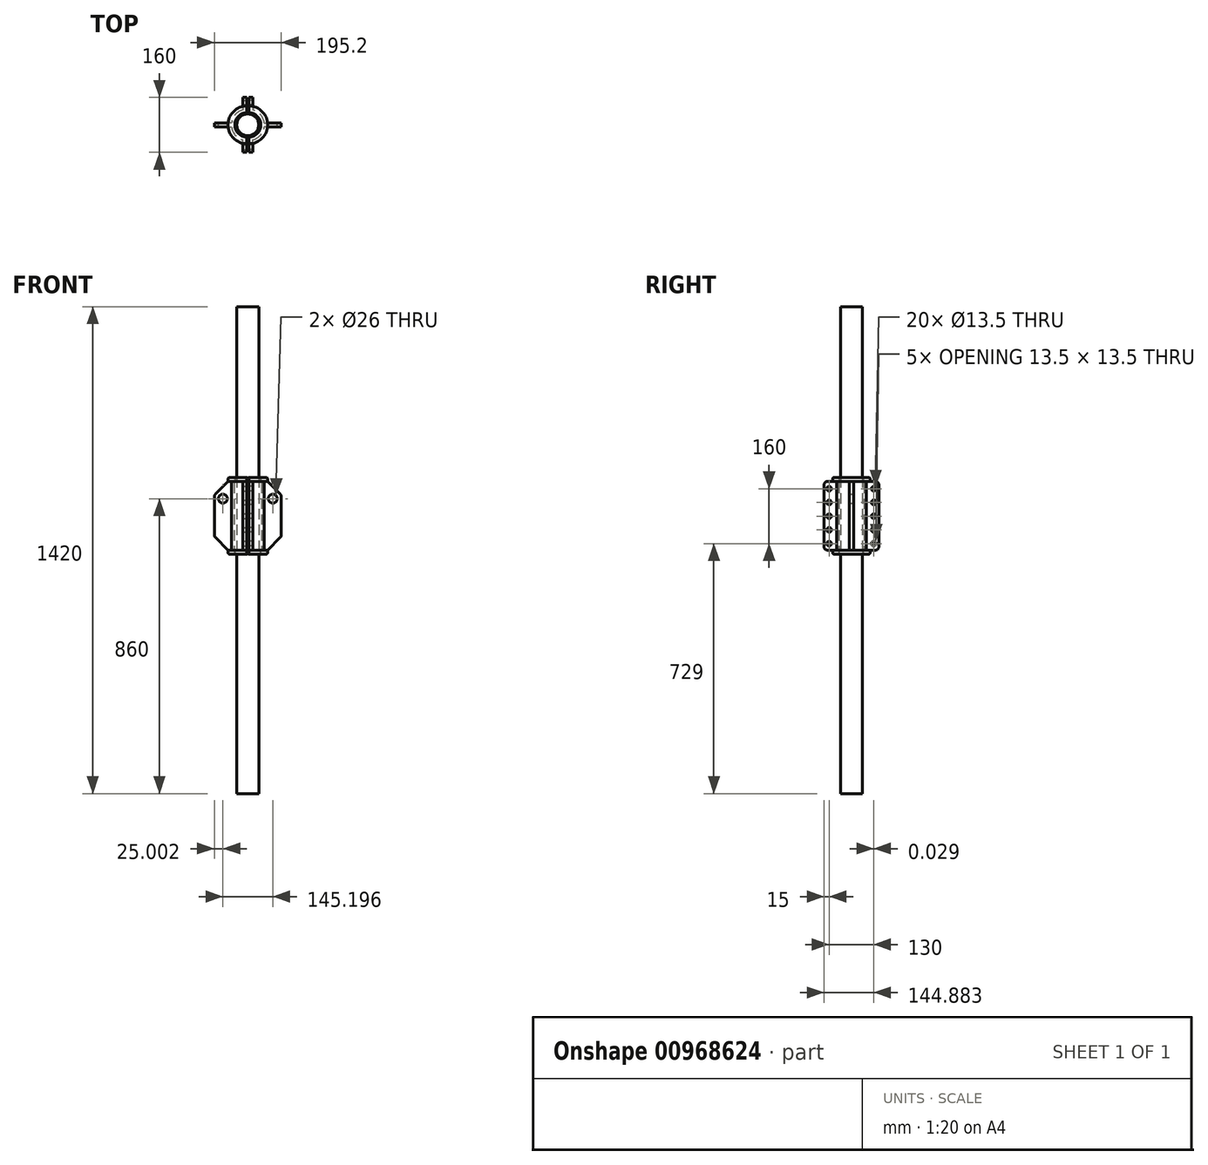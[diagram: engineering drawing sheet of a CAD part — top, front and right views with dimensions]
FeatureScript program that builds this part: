
annotation { "Feature Type Name" : "Feature", "Feature Type Description" : "" }
export const myFeature = defineFeature(function(context is Context, id is Id, definition is map)
    precondition{}
    {
        {
            var Q0;
            Q0=qCreatedBy(makeId("Top.planeOp"),FACE);
            var sketch = newSketch(context, id + "F0", { "sketchPlane" : qUnion([Q0])});
            skArc(sketch, "E0", {"start": v(0, -37) * mm, "mid": v(37, 0) * mm, "end": v(0, 37) * mm});
            skArc(sketch, "E1", {"start": v(0, -45) * mm, "mid": v(45, 0) * mm, "end": v(0, 45) * mm});
            skLineSegment(sketch, "E2", {"start": v(0, 45) * mm, "end": v(0, 37) * mm});
            skLineSegment(sketch, "E3", {"start": v(0, -37) * mm, "end": v(0, -45) * mm});
            skLineSegment(sketch, "E4", {"start": v(0, 45) * mm, "end": v(0, 80) * mm});
            skLineSegment(sketch, "E5", {"start": v(0, 80) * mm, "end": v(12, 80) * mm});
            skLineSegment(sketch, "E6", {"start": v(12, 80) * mm, "end": v(12, 43.37) * mm});
            skLineSegment(sketch, "E7", {"start": v(0, -45) * mm, "end": v(0, -80) * mm});
            skLineSegment(sketch, "E8", {"start": v(0, -80) * mm, "end": v(12, -80) * mm});
            skLineSegment(sketch, "E9", {"start": v(12, -80) * mm, "end": v(12, -43.37) * mm});
            skLineSegment(sketch, "E10", {"start": v(44.6, 6) * mm, "end": v(94.6, 6) * mm});
            skLineSegment(sketch, "E11", {"start": v(94.6, 6) * mm, "end": v(94.6, -6) * mm});
            skLineSegment(sketch, "E12", {"start": v(94.6, -6) * mm, "end": v(44.6, -6) * mm});
            skSolve(sketch);
        }
        {
            var Q0;
            Q0=makeQuery(id+"F0.imprint","IMPRINT",FACE,{"disambiguationData":[TD([[makeQuery(id+"F0.imprint","IMPRINT",EDGE,{"derivedFrom":sQuery(id+"F0.wireOp",EDGE,"E0")}),-1.0]])]});
            var Q1;
            {var subQ0=sQuery(id+"F0.wireOp",EDGE,"E4");Q1=makeQuery(id+"F0.imprint","IMPRINT",FACE,{"disambiguationData":[TD([[makeQuery(id+"F0.imprint","IMPRINT",EDGE,{"derivedFrom":subQ0}),-1.0]])]});}
            var Q2;
            {var subQ0=sQuery(id+"F0.wireOp",EDGE,"E10");Q2=makeQuery(id+"F0.imprint","IMPRINT",FACE,{"disambiguationData":[TD([[makeQuery(id+"F0.imprint","IMPRINT",EDGE,{"derivedFrom":subQ0}),-1.0]])]});}
            var Q3;
            {var subQ0=sQuery(id+"F0.wireOp",EDGE,"E7");Q3=makeQuery(id+"F0.imprint","IMPRINT",FACE,{"disambiguationData":[TD([[makeQuery(id+"F0.imprint","IMPRINT",EDGE,{"derivedFrom":subQ0}),1.0]])]});}
            extrude(context, id + "F1", {"entities" : qUnion([Q0, Q1, Q2, Q3]), "depth" : 200 * mm, "offsetDistance" : 25 * mm});
        }
        {
            var Q0;
            Q0=qCreatedBy(makeId("Right.planeOp"),FACE);
            var sketch = newSketch(context, id + "F2", { "sketchPlane" : qUnion([Q0])});
            skLineSegment(sketch, "E13", {"start": v(-65, 179) * mm, "end": v(-65, -10.82) * mm});
            skCircle(sketch, "E14", {"center": v(-65, 179) * mm, "radius": 7 * mm});
            skCircle(sketch, "E15.1.0.0", {"center": v(-64.97, 139) * mm, "radius": 7 * mm});
            skCircle(sketch, "E15.2.0.0", {"center": v(-64.94, 99) * mm, "radius": 7 * mm});
            skCircle(sketch, "E15.3.0.0", {"center": v(-64.91, 59) * mm, "radius": 7 * mm});
            skCircle(sketch, "E15.4.0.0", {"center": v(-64.88, 19) * mm, "radius": 7 * mm});
            skLineSegment(sketch, "E15.direction1", {"start": v(-65, 179) * mm, "end": v(-64.97, 139) * mm, "construction": true});
            skCircle(sketch, "E16.MirrorC", {"center": v(64.88, 19) * mm, "radius": 7 * mm});
            skCircle(sketch, "E17.MirrorC", {"center": v(64.91, 59) * mm, "radius": 7 * mm});
            skCircle(sketch, "E18.MirrorC", {"center": v(64.94, 99) * mm, "radius": 7 * mm});
            skCircle(sketch, "E19.MirrorC", {"center": v(64.97, 139) * mm, "radius": 7 * mm});
            skCircle(sketch, "E20.MirrorC", {"center": v(65, 179) * mm, "radius": 7 * mm});
            skSolve(sketch);
        }
        {
            var Q0;
            Q0=sQuery(id+"F2.wireOp",VERTEX,"E13.start");
            var Q1;
            Q1=sQuery(id+"F2.wireOp",VERTEX,"E15.direction1.end");
            var Q2;
            Q2=sQuery(id+"F2.wireOp",VERTEX,"E15.2.0.0.center");
            var Q3;
            Q3=sQuery(id+"F2.wireOp",VERTEX,"E15.3.0.0.center");
            var Q4;
            Q4=sQuery(id+"F2.wireOp",VERTEX,"E15.4.0.0.center");
            var Q5;
            Q5=sQuery(id+"F2.wireOp",VERTEX,"E20.MirrorC.center");
            var Q6;
            Q6=sQuery(id+"F2.wireOp",VERTEX,"E19.MirrorC.center");
            var Q7;
            Q7=sQuery(id+"F2.wireOp",VERTEX,"E18.MirrorC.center");
            var Q8;
            Q8=sQuery(id+"F2.wireOp",VERTEX,"E17.MirrorC.center");
            var Q9;
            Q9=sQuery(id+"F2.wireOp",VERTEX,"E16.MirrorC.center");
            var Q10;
            Q10=makeQuery(id+"F1.opExtrude","SWEPT_BODY",BODY,{"disambiguationData":[OSD([sQuery(id+"F0.wireOp",EDGE,"E0"),sQuery(id+"F0.wireOp",EDGE,"E1"),sQuery(id+"F0.wireOp",EDGE,"E2"),sQuery(id+"F0.wireOp",EDGE,"E3"),sQuery(id+"F0.wireOp",EDGE,"E4"),sQuery(id+"F0.wireOp",EDGE,"E5"),sQuery(id+"F0.wireOp",EDGE,"E6"),sQuery(id+"F0.wireOp",EDGE,"E7"),sQuery(id+"F0.wireOp",EDGE,"E8"),sQuery(id+"F0.wireOp",EDGE,"E9"),sQuery(id+"F0.wireOp",EDGE,"E10"),sQuery(id+"F0.wireOp",EDGE,"E11"),sQuery(id+"F0.wireOp",EDGE,"E12")])]});
            hole(context, id + "F3", {"style" : HoleStyle.SIMPLE, "endStyle" : HoleEndStyle.THROUGH, "oppositeDirection" : true, "standardTappedOrClearance" : lookupTablePath({ "fit" : "Normal", "standard" : "ISO", "size" : "M12", "type" : "Clearance" }), "standardBlindInLast" : lookupTablePath({ "fit" : "Normal", "standard" : "ISO", "engagement" : "75%", "pitch" : "1.75 mm", "size" : "M12", "type" : "Clearance & tapped" }), "holeDiameter" : 13.5 * mm, "majorDiameter" : 5 * mm, "isTappedThrough" : true, "tappedDepth" : 14.75 * mm, "tapClearance" : 3, "locations" : qUnion([Q0, Q1, Q2, Q3, Q4, Q5, Q6, Q7, Q8, Q9]), "scope" : qUnion([Q10])});
        }
        {
            var Q0;
            Q0=makeQuery(id+"F1.opExtrude","CAP_EDGE",EDGE,{"disambiguationData":[OSD([sQuery(id+"F0.wireOp",EDGE,"E11")])],"isStart":false});
            var Q1;
            Q1=makeQuery(id+"F1.opExtrude","CAP_EDGE",EDGE,{"disambiguationData":[OSD([sQuery(id+"F0.wireOp",EDGE,"E11")])],"isStart":true});
            chamfer(context, id + "F4", {"entities" : qUnion([Q0, Q1]), "width" : 40 * mm, "tangentPropagation" : true});
        }
        {
            var Q0;
            Q0=makeQuery(id+"F1.opExtrude","SWEPT_FACE",FACE,{"disambiguationData":[OSD([sQuery(id+"F0.wireOp",EDGE,"E10")])]});
            var sketch = newSketch(context, id + "F5", { "sketchPlane" : qUnion([Q0])});
            skCircle(sketch, "E21", {"center": v(-69.6, 150) * mm, "radius": 13 * mm});
            skSolve(sketch);
        }
        {
            var Q0;
            {var subQ0=sQuery(id+"F0.wireOp",EDGE,"E11");Q0=makeQuery(id+"F4.opChamfer","BLEND_EDGE",EDGE,{"blendedFrom":[makeQuery(id+"F1.opExtrude","CAP_EDGE",EDGE,{"disambiguationData":[OSD([subQ0])],"isStart":false}),makeQuery(id+"F1.opExtrude","SWEPT_FACE",FACE,{"disambiguationData":[OSD([subQ0])]})],"blendedInto":[makeQuery(id+"F1.opExtrude","SWEPT_FACE",FACE,{"disambiguationData":[OSD([subQ0])]})]});}
            var Q1;
            {var subQ0=sQuery(id+"F0.wireOp",EDGE,"E11");Q1=makeQuery(id+"F4.opChamfer","BLEND_EDGE",EDGE,{"blendedFrom":[makeQuery(id+"F1.opExtrude","CAP_EDGE",EDGE,{"disambiguationData":[OSD([subQ0])],"isStart":true}),makeQuery(id+"F1.opExtrude","SWEPT_FACE",FACE,{"disambiguationData":[OSD([subQ0])]})],"blendedInto":[makeQuery(id+"F1.opExtrude","SWEPT_FACE",FACE,{"disambiguationData":[OSD([subQ0])]})]});}
            fillet(context, id + "F6", {"entities" : qUnion([Q0, Q1]), "radius" : 10 * mm, "tangentPropagation" : true, "allowEdgeOverflow" : false});
        }
        {
            var Q0;
            Q0=qCreatedBy(makeId("Top.planeOp"),FACE);
            var sketch = newSketch(context, id + "F7", { "sketchPlane" : qUnion([Q0])});
            skArc(sketch, "E22", {"start": v(0, -55) * mm, "mid": v(55, 0) * mm, "end": v(0, 55) * mm});
            skArc(sketch, "E23", {"start": v(0, -35) * mm, "mid": v(35, 0) * mm, "end": v(0, 35) * mm});
            skLineSegment(sketch, "E24", {"start": v(0, -35) * mm, "end": v(0, -55) * mm});
            skLineSegment(sketch, "E25", {"start": v(0, 55) * mm, "end": v(0, 35) * mm});
            skSolve(sketch);
        }
        {
            var Q0;
            Q0=makeQuery(id+"F7.imprint","IMPRINT",FACE,{"disambiguationData":[TD([[makeQuery(id+"F7.imprint","IMPRINT",EDGE,{"derivedFrom":sQuery(id+"F7.wireOp",EDGE,"E22")}),1.0]])]});
            extrude(context, id + "F8", {"entities" : qUnion([Q0]), "operationType" : NewBodyOperationType.ADD, "oppositeDirection" : true, "depth" : 12 * mm, "offsetDistance" : 25 * mm});
        }
        {
            var Q0;
            Q0=makeQuery(id+"F1.opExtrude","CAP_FACE",FACE,{"disambiguationData":[OSD([sQuery(id+"F0.wireOp",EDGE,"E0"),sQuery(id+"F0.wireOp",EDGE,"E1"),sQuery(id+"F0.wireOp",EDGE,"E2"),sQuery(id+"F0.wireOp",EDGE,"E3"),sQuery(id+"F0.wireOp",EDGE,"E4"),sQuery(id+"F0.wireOp",EDGE,"E5"),sQuery(id+"F0.wireOp",EDGE,"E6"),sQuery(id+"F0.wireOp",EDGE,"E7"),sQuery(id+"F0.wireOp",EDGE,"E8"),sQuery(id+"F0.wireOp",EDGE,"E9"),sQuery(id+"F0.wireOp",EDGE,"E10"),sQuery(id+"F0.wireOp",EDGE,"E11"),sQuery(id+"F0.wireOp",EDGE,"E12")])],"isStart":false});
            cPlane(context, id + "F9", {"entities" : qUnion([Q0]), "cplaneType" : CPlaneType.OFFSET, "offset" : 0 * mm, "width" : 150 * mm, "height" : 150 * mm});
        }
        {
            var Q0;
            Q0=qCreatedBy(id+"F9.planeOp",FACE);
            var sketch = newSketch(context, id + "F10", { "sketchPlane" : qUnion([Q0])});
            skArc(sketch, "E26", {"start": v(0, -55) * mm, "mid": v(55, 0) * mm, "end": v(0, 55) * mm});
            skArc(sketch, "E27", {"start": v(0, -35) * mm, "mid": v(35, 0) * mm, "end": v(0, 35) * mm});
            skLineSegment(sketch, "E28", {"start": v(0, -35) * mm, "end": v(0, -55) * mm});
            skLineSegment(sketch, "E29", {"start": v(0, 55) * mm, "end": v(0, 35) * mm});
            skSolve(sketch);
        }
        {
            var Q0;
            Q0=makeQuery(id+"F10.imprint","IMPRINT",FACE,{"disambiguationData":[TD([[makeQuery(id+"F10.imprint","IMPRINT",EDGE,{"derivedFrom":sQuery(id+"F10.wireOp",EDGE,"E26")}),1.0]])]});
            extrude(context, id + "F11", {"entities" : qUnion([Q0]), "operationType" : NewBodyOperationType.ADD, "depth" : 12 * mm, "offsetDistance" : 25 * mm});
        }
        {
            var Q0;
            Q0=sQuery(id+"F5.wireOp",VERTEX,"E21.center");
            var Q1;
            Q1=makeQuery(id+"F1.opExtrude","SWEPT_BODY",BODY,{"disambiguationData":[OSD([sQuery(id+"F0.wireOp",EDGE,"E0"),sQuery(id+"F0.wireOp",EDGE,"E1"),sQuery(id+"F0.wireOp",EDGE,"E2"),sQuery(id+"F0.wireOp",EDGE,"E3"),sQuery(id+"F0.wireOp",EDGE,"E4"),sQuery(id+"F0.wireOp",EDGE,"E5"),sQuery(id+"F0.wireOp",EDGE,"E6"),sQuery(id+"F0.wireOp",EDGE,"E7"),sQuery(id+"F0.wireOp",EDGE,"E8"),sQuery(id+"F0.wireOp",EDGE,"E9"),sQuery(id+"F0.wireOp",EDGE,"E10"),sQuery(id+"F0.wireOp",EDGE,"E11"),sQuery(id+"F0.wireOp",EDGE,"E12")])]});
            hole(context, id + "F12", {"style" : HoleStyle.SIMPLE, "endStyle" : HoleEndStyle.THROUGH, "standardTappedOrClearance" : lookupTablePath({ "fit" : "Normal", "standard" : "ISO", "size" : "M24", "type" : "Clearance" }), "standardBlindInLast" : lookupTablePath({ "fit" : "Normal", "standard" : "ISO", "engagement" : "75%", "pitch" : "2 mm", "size" : "M24", "type" : "Clearance & tapped" }), "holeDiameter" : 26 * mm, "majorDiameter" : 5 * mm, "isTappedThrough" : true, "tappedDepth" : 14.75 * mm, "tapClearance" : 3, "locations" : qUnion([Q0]), "scope" : qUnion([Q1])});
        }
        {
            var Q0;
            Q0=makeQuery(id+"F1.opExtrude","CAP_EDGE",EDGE,{"disambiguationData":[OSD([sQuery(id+"F0.wireOp",EDGE,"E8")])],"isStart":false});
            var Q1;
            Q1=makeQuery(id+"F1.opExtrude","CAP_EDGE",EDGE,{"disambiguationData":[OSD([sQuery(id+"F0.wireOp",EDGE,"E5")])],"isStart":false});
            var Q2;
            Q2=makeQuery(id+"F1.opExtrude","CAP_EDGE",EDGE,{"disambiguationData":[OSD([sQuery(id+"F0.wireOp",EDGE,"E5")])],"isStart":true});
            var Q3;
            Q3=makeQuery(id+"F1.opExtrude","CAP_EDGE",EDGE,{"disambiguationData":[OSD([sQuery(id+"F0.wireOp",EDGE,"E8")])],"isStart":true});
            fillet(context, id + "F13", {"entities" : qUnion([Q0, Q1, Q2, Q3]), "radius" : 10 * mm, "tangentPropagation" : true, "allowEdgeOverflow" : false});
        }
        {
            var Q0;
            {var subQ0=makeQuery(id+"F1.opExtrude","CAP_EDGE",EDGE,{"disambiguationData":[OSD([sQuery(id+"F0.wireOp",EDGE,"E0")])],"isStart":false});Q0=makeQuery(id+"FrsH2Kbrjr3JI1j_1.boolean.opBoolean","MERGE",EDGE,{"derivedFrom":[subQ0,makeQuery(id+"FrsH2Kbrjr3JI1j_1.opPattern","COPY",EDGE,{"derivedFrom":subQ0,"instanceName":"1"})]});}
            var Q1;
            {var subQ0=makeQuery(id+"F11.opExtrude","CAP_EDGE",EDGE,{"disambiguationData":[OSD([sQuery(id+"F10.wireOp",EDGE,"E27")])],"isStart":false});Q1=makeQuery(id+"FrsH2Kbrjr3JI1j_1.boolean.opBoolean","MERGE",EDGE,{"derivedFrom":[subQ0,makeQuery(id+"FrsH2Kbrjr3JI1j_1.opPattern","COPY",EDGE,{"derivedFrom":subQ0,"instanceName":"1"})]});}
            var Q2;
            {var subQ0=makeQuery(id+"F11.opExtrude","CAP_EDGE",EDGE,{"disambiguationData":[OSD([sQuery(id+"F10.wireOp",EDGE,"E26")])],"isStart":false});Q2=makeQuery(id+"FrsH2Kbrjr3JI1j_1.boolean.opBoolean","MERGE",EDGE,{"derivedFrom":[subQ0,makeQuery(id+"FrsH2Kbrjr3JI1j_1.opPattern","COPY",EDGE,{"derivedFrom":subQ0,"instanceName":"1"})]});}
            var Q3;
            {var subQ0=makeQuery(id+"F1.opExtrude","CAP_EDGE",EDGE,{"disambiguationData":[OSD([sQuery(id+"F0.wireOp",EDGE,"E0")])],"isStart":true});Q3=makeQuery(id+"FrsH2Kbrjr3JI1j_1.boolean.opBoolean","MERGE",EDGE,{"derivedFrom":[subQ0,makeQuery(id+"FrsH2Kbrjr3JI1j_1.opPattern","COPY",EDGE,{"derivedFrom":subQ0,"instanceName":"1"})]});}
            var Q4;
            {var subQ0=makeQuery(id+"F8.opExtrude","CAP_EDGE",EDGE,{"disambiguationData":[OSD([sQuery(id+"F7.wireOp",EDGE,"E23")])],"isStart":false});Q4=makeQuery(id+"FrsH2Kbrjr3JI1j_1.boolean.opBoolean","MERGE",EDGE,{"derivedFrom":[subQ0,makeQuery(id+"FrsH2Kbrjr3JI1j_1.opPattern","COPY",EDGE,{"derivedFrom":subQ0,"instanceName":"1"})]});}
            var Q5;
            {var subQ0=makeQuery(id+"F8.opExtrude","CAP_EDGE",EDGE,{"disambiguationData":[OSD([sQuery(id+"F7.wireOp",EDGE,"E22")])],"isStart":false});Q5=makeQuery(id+"FrsH2Kbrjr3JI1j_1.boolean.opBoolean","MERGE",EDGE,{"derivedFrom":[subQ0,makeQuery(id+"FrsH2Kbrjr3JI1j_1.opPattern","COPY",EDGE,{"derivedFrom":subQ0,"instanceName":"1"})]});}
            fillet(context, id + "F14", {"entities" : qUnion([Q0, Q1, Q2, Q3, Q4, Q5]), "radius" : 5 * mm, "tangentPropagation" : true, "allowEdgeOverflow" : false});
        }
        {
            var Q0;
            Q0=qCreatedBy(makeId("Right.planeOp"),FACE);
            cPlane(context, id + "F15", {"entities" : qUnion([Q0]), "cplaneType" : CPlaneType.OFFSET, "offset" : 3 * mm, "oppositeDirection" : true, "width" : 150 * mm, "height" : 150 * mm});
        }
        {
            var Q0;
            Q0=makeQuery(id+"F1.opExtrude","SWEPT_BODY",BODY,{"disambiguationData":[OSD([sQuery(id+"F0.wireOp",EDGE,"E0"),sQuery(id+"F0.wireOp",EDGE,"E1"),sQuery(id+"F0.wireOp",EDGE,"E2"),sQuery(id+"F0.wireOp",EDGE,"E3"),sQuery(id+"F0.wireOp",EDGE,"E4"),sQuery(id+"F0.wireOp",EDGE,"E5"),sQuery(id+"F0.wireOp",EDGE,"E6"),sQuery(id+"F0.wireOp",EDGE,"E7"),sQuery(id+"F0.wireOp",EDGE,"E8"),sQuery(id+"F0.wireOp",EDGE,"E9"),sQuery(id+"F0.wireOp",EDGE,"E10"),sQuery(id+"F0.wireOp",EDGE,"E11"),sQuery(id+"F0.wireOp",EDGE,"E12")])]});
            var Q1;
            Q1=qCreatedBy(id+"F15.planeOp",FACE);
            mirror(context, id + "F16", {"entities" : qUnion([Q0]), "mirrorPlane" : qUnion([Q1])});
        }
        {
            var Q0;
            Q0=qCreatedBy(makeId("Top.planeOp"),FACE);
            var sketch = newSketch(context, id + "F17", { "sketchPlane" : qUnion([Q0])});
            skCircle(sketch, "E30", {"center": v(-3.14, 0) * mm, "radius": 32 * mm});
            skSolve(sketch);
        }
        {
            var Q0;
            Q0=makeQuery(id+"F17.imprint","IMPRINT",FACE,{"disambiguationData":[TD([[makeQuery(id+"F17.imprint","IMPRINT",EDGE,{"derivedFrom":sQuery(id+"F17.wireOp",EDGE,"E30")}),1.0]])]});
            extrude(context, id + "F18", {"entities" : qUnion([Q0]), "endBound" : BoundingType.SYMMETRIC, "depth" : 1420 * mm, "offsetDistance" : 25 * mm});
        }
    });
